# Revit family: SRSH-B
name_source: partatom
category: Mechanical Equipment
units: mm (PartAtom-declared; Revit-internal decimal feet)

## family parameters
Always vertical = Yes
Cut with Voids When Loaded = No
Part Type = Normal
Room Calculation Point = No
Round Connector Dimension = Use Diameter
Shared = No
Work Plane-Based = No

## types (14) — shared parameters
0 = 0' - 0"
1" = 0' - 1"
1.5 = 0' - 1 1/2"
2" = 0' - 2"
2' = 2' - 0"
3" = 0' - 3"
4" = 0' - 4"
45 = 55.00°
Manufacturer = Loren Cook Company
Model = SRSH-B
ONE EIGTH = 0' - 0 1/8"
Type Comments = Tamper Proof Downblast Centrifugal Exhaust Ventilator Roof Mounted/Belt Drive
URL = www.lorencook.com

## per-type parameters (varying)
| type | (G+F+F)/2 | -(G+F+F)/2 | -C/2 | A | A-B-E-F | A/2 | B | B/2 | C | C/2 | D | E | F | G | G/2 | RO | RO/2 | T_SQ | T_SQ/2 | T_SQ/2+.125" |
| 60_SRSH-B | 0' - 10 3/32" | -0' - 10 3/32" | -1' - 2 5/8" | 1' - 11 7/16" | 0' - 7 3/32" | 0' - 11 23/32" | 0' - 1" | 0' - 0 1/2" | 2' - 5 1/4" | 1' - 2 5/8" | 0' - 2" | 0' - 11 25/32" | 0' - 3 9/16" | 1' - 1 1/16" | 0' - 6 17/32" | 1' - 1 1/2" | 0' - 6 3/4" | 1' - 6 1/4" | 0' - 9 1/8" | 0' - 9 1/4" |
| 70_SRSH-B | 0' - 10 3/32" | -0' - 10 3/32" | -1' - 2 5/8" | 1' - 11 7/16" | 0' - 7 3/32" | 0' - 11 23/32" | 0' - 1" | 0' - 0 1/2" | 2' - 5 1/4" | 1' - 2 5/8" | 0' - 2" | 0' - 11 25/32" | 0' - 3 9/16" | 1' - 1 1/16" | 0' - 6 17/32" | 1' - 1 1/2" | 0' - 6 3/4" | 1' - 6 1/4" | 0' - 9 1/8" | 0' - 9 1/4" |
| 80_SRSH-B | 0' - 10 3/32" | -0' - 10 3/32" | -1' - 2 5/8" | 1' - 11 7/16" | 0' - 7 3/32" | 0' - 11 23/32" | 0' - 1" | 0' - 0 1/2" | 2' - 5 1/4" | 1' - 2 5/8" | 0' - 2" | 0' - 11 25/32" | 0' - 3 9/16" | 1' - 1 1/16" | 0' - 6 17/32" | 1' - 1 1/2" | 0' - 6 3/4" | 1' - 6 1/4" | 0' - 9 1/8" | 0' - 9 1/4" |
| 100_SRSH-B | 0' - 10 3/32" | -0' - 10 3/32" | -1' - 2 5/8" | 1' - 11 7/16" | 0' - 7 3/32" | 0' - 11 23/32" | 0' - 1" | 0' - 0 1/2" | 2' - 5 1/4" | 1' - 2 5/8" | 0' - 2" | 0' - 11 25/32" | 0' - 3 9/16" | 1' - 1 1/16" | 0' - 6 17/32" | 1' - 1 1/2" | 0' - 6 3/4" | 1' - 6 1/4" | 0' - 9 1/8" | 0' - 9 1/4" |
| 120_SRSH-B | 0' - 11 1/8" | -0' - 11 1/8" | -1' - 4 11/32" | 2' - 0 11/16" | 0' - 8 5/16" | 1' - 0 11/32" | 0' - 1" | 0' - 0 1/2" | 2' - 8 11/16" | 1' - 4 11/32" | 0' - 2" | 0' - 10 25/32" | 0' - 4 19/32" | 1' - 1 1/16" | 0' - 6 17/32" | 1' - 3 1/2" | 0' - 7 3/4" | 1' - 8 1/4" | 0' - 10 1/8" | 0' - 10 1/4" |
| 135_SRSH-B | 0' - 11 1/8" | -0' - 11 1/8" | -1' - 4 7/8" | 2' - 1 5/8" | 0' - 9 1/4" | 1' - 0 13/16" | 0' - 1" | 0' - 0 1/2" | 2' - 9 3/4" | 1' - 4 7/8" | 0' - 2" | 0' - 10 25/32" | 0' - 4 19/32" | 1' - 1 1/16" | 0' - 6 17/32" | 1' - 3 1/2" | 0' - 7 3/4" | 1' - 8 1/4" | 0' - 10 1/8" | 0' - 10 1/4" |
| 150_SRSH-B | 1' - 1 1/8" | -1' - 1 1/8" | -1' - 7 13/32" | 2' - 5 9/16" | 0' - 10 1/4" | 1' - 2 25/32" | 0' - 1" | 0' - 0 1/2" | 3' - 2 13/16" | 1' - 7 13/32" | 0' - 2" | 1' - 1 7/32" | 0' - 5 3/32" | 1' - 4 1/16" | 0' - 8 1/32" | 1' - 7 1/2" | 0' - 9 3/4" | 2' - 0 1/4" | 1' - 0 1/8" | 1' - 0 1/4" |
| 165_SRSH-B | 1' - 1 1/8" | -1' - 1 1/8" | -1' - 7 31/32" | 2' - 6 1/2" | 0' - 11 3/16" | 1' - 3 1/4" | 0' - 1" | 0' - 0 1/2" | 3' - 3 15/16" | 1' - 7 31/32" | 0' - 2" | 1' - 1 7/32" | 0' - 5 3/32" | 1' - 4 1/16" | 0' - 8 1/32" | 1' - 7 1/2" | 0' - 9 3/4" | 2' - 0 1/4" | 1' - 0 1/8" | 1' - 0 1/4" |
| 180_SRSH-B | 1' - 4 1/8" | -1' - 4 1/8" | -1' - 11 25/32" | 3' - 0 7/16" | 1' - 0 19/32" | 1' - 6 7/32" | 0' - 1 1/2" | 0' - 0 3/4" | 3' - 11 9/16" | 1' - 11 25/32" | 0' - 3" | 1' - 4 1/4" | 0' - 6 3/32" | 1' - 8 1/16" | 0' - 10 1/32" | 2' - 1 1/2" | 1' - 0 3/4" | 2' - 6 1/4" | 1' - 3 1/8" | 1' - 3 1/4" |
| 195_SRSH-B | 1' - 4 1/8" | -1' - 4 1/8" | -2' - 0 11/32" | 3' - 1 3/8" | 1' - 1 17/32" | 1' - 6 11/16" | 0' - 1 1/2" | 0' - 0 3/4" | 4' - 0 11/16" | 2' - 0 11/32" | 0' - 3" | 1' - 4 1/4" | 0' - 6 3/32" | 1' - 8 1/16" | 0' - 10 1/32" | 2' - 1 1/2" | 1' - 0 3/4" | 2' - 6 1/4" | 1' - 3 1/8" | 1' - 3 1/4" |
| 210_SRSH-B | 1' - 4 1/8" | -1' - 4 1/8" | -2' - 0 7/8" | 3' - 2 5/16" | 1' - 2 15/32" | 1' - 7 5/32" | 0' - 1 1/2" | 0' - 0 3/4" | 4' - 1 3/4" | 2' - 0 7/8" | 0' - 3" | 1' - 4 1/4" | 0' - 6 3/32" | 1' - 8 1/16" | 0' - 10 1/32" | 2' - 1 1/2" | 1' - 0 3/4" | 2' - 6 1/4" | 1' - 3 1/8" | 1' - 3 1/4" |
| 225_SRSH-B | 1' - 4 1/8" | -1' - 4 1/8" | -2' - 1 13/32" | 3' - 3 1/4" | 1' - 3 13/32" | 1' - 7 5/8" | 0' - 1 1/2" | 0' - 0 3/4" | 4' - 2 13/16" | 2' - 1 13/32" | 0' - 3" | 1' - 4 1/4" | 0' - 6 3/32" | 1' - 8 1/16" | 0' - 10 1/32" | 2' - 1 1/2" | 1' - 0 3/4" | 2' - 6 1/4" | 1' - 3 1/8" | 1' - 3 1/4" |
| 245_SRSH-B | 1' - 4 1/8" | -1' - 4 1/8" | -2' - 2 1/8" | 3' - 4 1/2" | 1' - 4 21/32" | 1' - 8 1/4" | 0' - 1 1/2" | 0' - 0 3/4" | 4' - 4 1/4" | 2' - 2 1/8" | 0' - 3" | 1' - 4 1/4" | 0' - 6 3/32" | 1' - 8 1/16" | 0' - 10 1/32" | 2' - 1 1/2" | 1' - 0 3/4" | 2' - 6 1/4" | 1' - 3 1/8" | 1' - 3 1/4" |
| 270_SRSH-B | 1' - 7 1/8" | -1' - 7 1/8" | -2' - 6" | 3' - 10" | 1' - 6 5/32" | 1' - 11" | 0' - 1 1/2" | 0' - 0 3/4" | 5' - 0" | 2' - 6" | 0' - 3" | 1' - 7 1/4" | 0' - 7 3/32" | 2' - 0 1/16" | 1' - 0 1/32" | 1' - 7 5/16" | 0' - 9 21/32" | 2' - 0 1/16" | 1' - 0 1/32" | 1' - 0 5/32" |

## geometry (parser evidence)
native form markers: Sweep x2
no freeform markers — native parametric forms only
